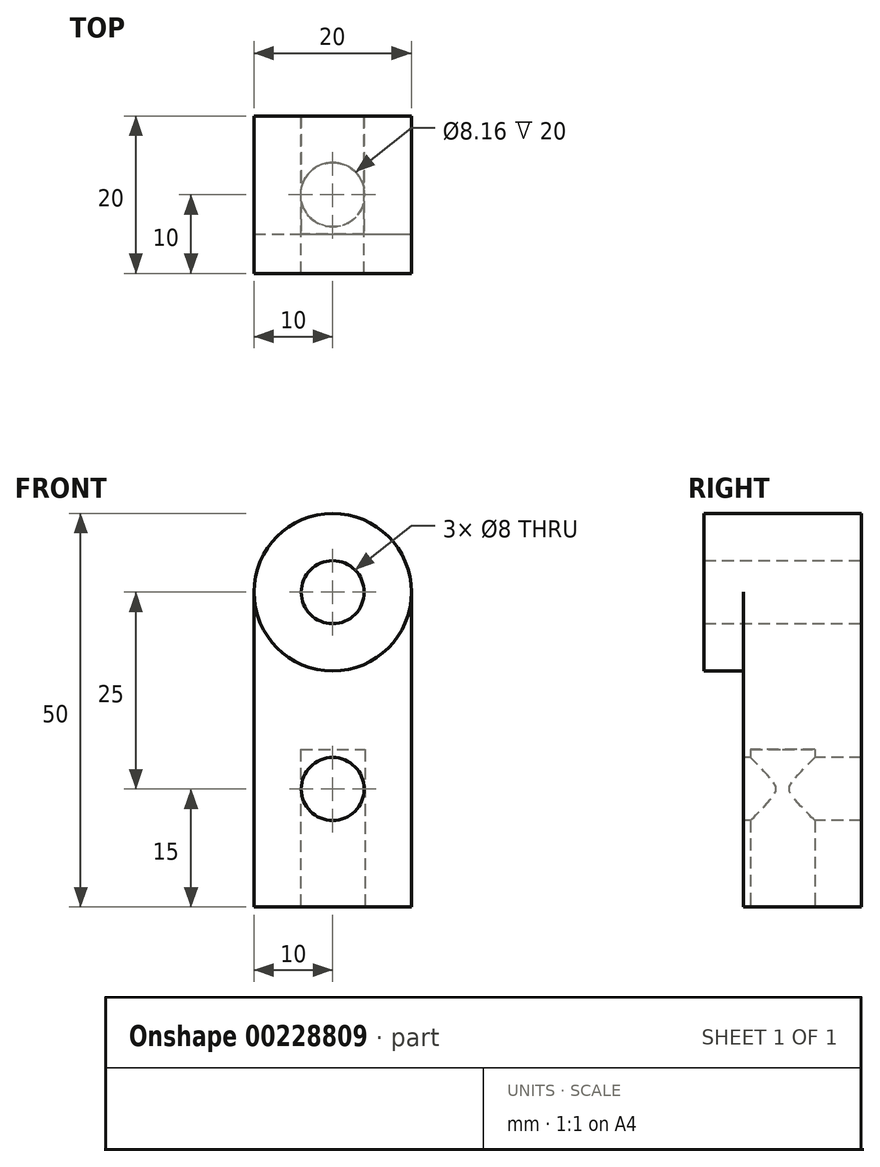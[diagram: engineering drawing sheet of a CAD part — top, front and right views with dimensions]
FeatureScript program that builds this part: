
annotation { "Feature Type Name" : "Feature", "Feature Type Description" : "" }
export const myFeature = defineFeature(function(context is Context, id is Id, definition is map)
    precondition{}
    {
        {
            var Q0;
            Q0=qCreatedBy(makeId("Front.planeOp"),FACE);
            var sketch = newSketch(context, id + "F0", { "sketchPlane" : qUnion([Q0])});
            skLineSegment(sketch, "E0.bottom", {"start": v(-10, 15) * mm, "end": v(10, 15) * mm});
            skLineSegment(sketch, "E0.top", {"start": v(-10, -35) * mm, "end": v(10, -35) * mm});
            skLineSegment(sketch, "E0.left", {"start": v(-10, 15) * mm, "end": v(-10, -35) * mm});
            skLineSegment(sketch, "E0.right", {"start": v(10, 15) * mm, "end": v(10, -35) * mm});
            skCircle(sketch, "E1", {"center": v(0, 5) * mm, "radius": 4 * mm});
            skSolve(sketch);
        }
        {
            var Q0;
            Q0=makeQuery(id+"F0.imprint","IMPRINT",FACE,{"disambiguationData":[TD([[makeQuery(id+"F0.imprint","IMPRINT",EDGE,{"derivedFrom":sQuery(id+"F0.wireOp",EDGE,"E0.bottom")}),-1.0]])]});
            extrude(context, id + "F1", {"entities" : qUnion([Q0]), "depth" : 10 * mm, "hasSecondDirection" : true, "secondDirectionOppositeDirection" : true, "secondDirectionDepth" : 10 * mm});
        }
        {
            var Q0;
            Q0=makeQuery(id+"F1.opExtrude","SWEPT_EDGE",EDGE,{"disambiguationData":[OSD([sQuery(id+"F0.wireOp",EDGE,"E0.bottom"),sQuery(id+"F0.wireOp",EDGE,"E0.left")])]});
            var Q1;
            Q1=makeQuery(id+"F1.opExtrude","SWEPT_EDGE",EDGE,{"disambiguationData":[OSD([sQuery(id+"F0.wireOp",EDGE,"E0.bottom"),sQuery(id+"F0.wireOp",EDGE,"E0.right")])]});
            fillet(context, id + "F2", {"entities" : qUnion([Q0, Q1]), "radius" : 10 * mm, "tangentPropagation" : true, "allowEdgeOverflow" : false});
        }
        {
            var Q0;
            Q0=makeQuery(id+"F1.opExtrude","SWEPT_FACE",FACE,{"disambiguationData":[OSD([sQuery(id+"F0.wireOp",EDGE,"E0.top")])]});
            var sketch = newSketch(context, id + "F3", { "sketchPlane" : qUnion([Q0])});
            skCircle(sketch, "E2", {"center": v(0, 0) * mm, "radius": 4.08 * mm});
            skSolve(sketch);
        }
        {
            var Q0;
            Q0 = qSketchRegion(id + "F3", true);
            extrude(context, id + "F4", {"entities" : qUnion([Q0]), "operationType" : NewBodyOperationType.REMOVE, "oppositeDirection" : true, "depth" : 20 * mm});
        }
        {
            var Q0;
            Q0=makeQuery(id+"F1.opExtrude","CAP_FACE",FACE,{"disambiguationData":[OSD([sQuery(id+"F0.wireOp",EDGE,"E0.bottom"),sQuery(id+"F0.wireOp",EDGE,"E0.top"),sQuery(id+"F0.wireOp",EDGE,"E0.left"),sQuery(id+"F0.wireOp",EDGE,"E0.right"),sQuery(id+"F0.wireOp",EDGE,"E1")])],"isStart":false});
            var sketch = newSketch(context, id + "F5", { "sketchPlane" : qUnion([Q0])});
            skCircle(sketch, "E3", {"center": v(0, -20) * mm, "radius": 4 * mm});
            skSolve(sketch);
        }
        {
            var Q0;
            Q0=sQuery(id+"F5.wireOp",VERTEX,"E3.center");
            var Q1;
            Q1=makeQuery(id+"F1.opExtrude","SWEPT_BODY",BODY,{"disambiguationData":[OSD([sQuery(id+"F0.wireOp",EDGE,"E0.bottom"),sQuery(id+"F0.wireOp",EDGE,"E0.top"),sQuery(id+"F0.wireOp",EDGE,"E0.left"),sQuery(id+"F0.wireOp",EDGE,"E0.right"),sQuery(id+"F0.wireOp",EDGE,"E1")])]});
            hole(context, id + "F6", {"style" : HoleStyle.SIMPLE, "endStyle" : HoleEndStyle.THROUGH, "holeDiameter" : 8 * mm, "locations" : qUnion([Q0]), "scope" : qUnion([Q1]), "isTappedThrough" : true});
        }
        {
            var Q0;
            Q0=makeQuery(id+"F1.opExtrude","CAP_FACE",FACE,{"disambiguationData":[OSD([sQuery(id+"F0.wireOp",EDGE,"E0.bottom"),sQuery(id+"F0.wireOp",EDGE,"E0.top"),sQuery(id+"F0.wireOp",EDGE,"E0.left"),sQuery(id+"F0.wireOp",EDGE,"E0.right"),sQuery(id+"F0.wireOp",EDGE,"E1")])],"isStart":false});
            var sketch = newSketch(context, id + "F7", { "sketchPlane" : qUnion([Q0])});
            skCircle(sketch, "E4", {"center": v(0, 5) * mm, "radius": 10 * mm});
            skLineSegment(sketch, "E5.bottom", {"start": v(-10, 5) * mm, "end": v(10, 5) * mm});
            skLineSegment(sketch, "E5.top", {"start": v(-10, -35) * mm, "end": v(10, -35) * mm});
            skLineSegment(sketch, "E5.left", {"start": v(-10, 5) * mm, "end": v(-10, -35) * mm});
            skLineSegment(sketch, "E5.right", {"start": v(10, 5) * mm, "end": v(10, -35) * mm});
            skSolve(sketch);
        }
        {
            var Q0;
            Q0=makeQuery(id+"F7.imprint","IMPRINT",FACE,{"disambiguationData":[TD([[makeQuery(id+"F7.imprint","IMPRINT",EDGE,{"derivedFrom":sQuery(id+"F7.wireOp",EDGE,"E5.top")}),1.0]])]});
            extrude(context, id + "F8", {"entities" : qUnion([Q0]), "operationType" : NewBodyOperationType.REMOVE, "oppositeDirection" : true, "depth" : 5 * mm});
        }
    });
